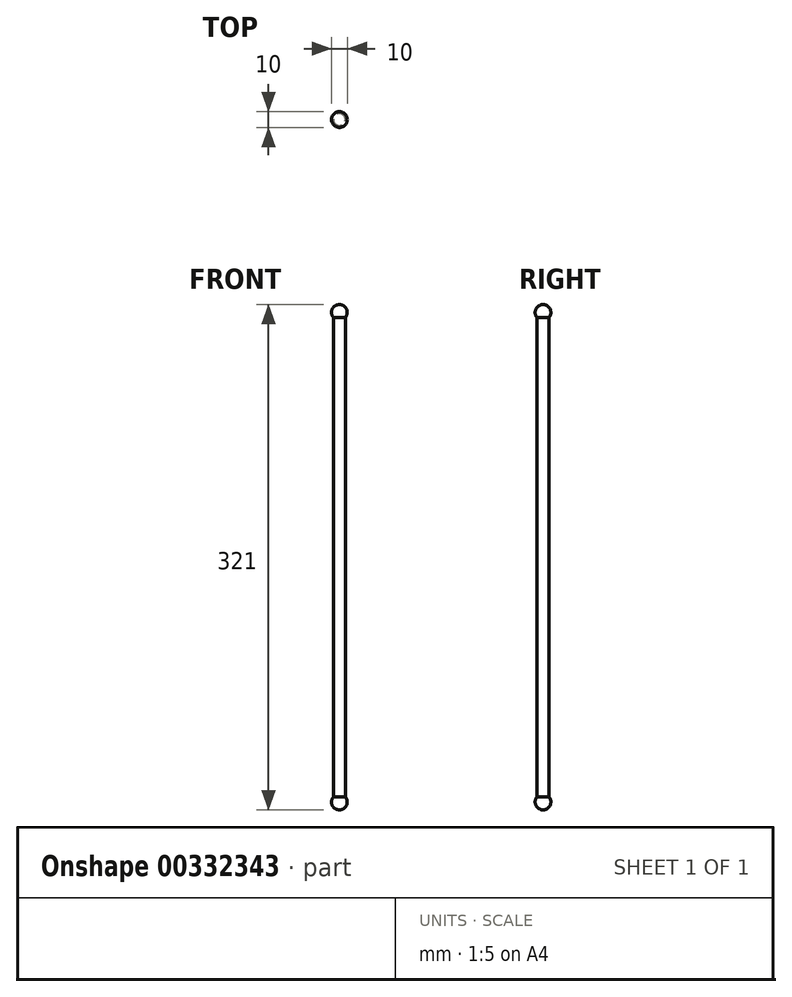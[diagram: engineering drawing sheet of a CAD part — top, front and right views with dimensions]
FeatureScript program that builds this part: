
annotation { "Feature Type Name" : "Feature", "Feature Type Description" : "" }
export const myFeature = defineFeature(function(context is Context, id is Id, definition is map)
    precondition{}
    {
        {
            var Q0;
            Q0=qCreatedBy(makeId("Top.planeOp"),FACE);
            var sketch = newSketch(context, id + "F0", { "sketchPlane" : qUnion([Q0])});
            skCircle(sketch, "E0", {"center": v(0, 0) * mm, "radius": 3.8 * mm});
            skSolve(sketch);
        }
        {
            var Q0;
            Q0=makeQuery(id+"F0.imprint","IMPRINT",FACE,{"disambiguationData":[TD([[makeQuery(id+"F0.imprint","IMPRINT",EDGE,{"derivedFrom":sQuery(id+"F0.wireOp",EDGE,"E0")}),1.0]])]});
            extrude(context, id + "F1", {"entities" : qUnion([Q0]), "depth" : 305 * mm});
        }
        {
            var Q0;
            Q0=makeQuery(id+"F1.opExtrude","CAP_FACE",FACE,{"disambiguationData":[OSD([sQuery(id+"F0.wireOp",EDGE,"E0")])],"isStart":false});
            cPlane(context, id + "F2", {"entities" : qUnion([Q0]), "cplaneType" : CPlaneType.OFFSET, "offset" : 3 * mm, "width" : 150 * mm, "height" : 150 * mm});
        }
        {
            var Q0;
            Q0=qCreatedBy(id+"F2.planeOp",FACE);
            var sketch = newSketch(context, id + "F3", { "sketchPlane" : qUnion([Q0])});
            skCircle(sketch, "E1", {"center": v(0, 0) * mm, "radius": 5 * mm});
            skLineSegment(sketch, "E2", {"start": v(0, 5) * mm, "end": v(0, -5) * mm});
            skSolve(sketch);
        }
        {
            var Q0;
            {var subQ0=sQuery(id+"F3.wireOp",EDGE,"E2");Q0=makeQuery(id+"F3.imprint","IMPRINT",FACE,{"disambiguationData":[TD([[makeQuery(id+"F3.imprint","IMPRINT",EDGE,{"derivedFrom":subQ0}),-1.0]])]});}
            var Q1;
            Q1=sQuery(id+"F3.wireOp",EDGE,"E2");
            revolve(context, id + "F4", {"operationType" : NewBodyOperationType.ADD, "entities" : qUnion([Q0]), "axis" : qUnion([Q1]), "revolveType" : RevolveType.FULL});
        }
        {
            var Q0;
            Q0=makeQuery(id+"F1.opExtrude","CAP_FACE",FACE,{"disambiguationData":[OSD([sQuery(id+"F0.wireOp",EDGE,"E0")])],"isStart":true});
            cPlane(context, id + "F5", {"entities" : qUnion([Q0]), "cplaneType" : CPlaneType.OFFSET, "offset" : 3 * mm, "width" : 150 * mm, "height" : 150 * mm});
        }
        {
            var Q0;
            Q0=qCreatedBy(id+"F5.planeOp",FACE);
            var sketch = newSketch(context, id + "F6", { "sketchPlane" : qUnion([Q0])});
            skCircle(sketch, "E3", {"center": v(0, 0) * mm, "radius": 5 * mm});
            skLineSegment(sketch, "E4", {"start": v(0, 5) * mm, "end": v(0, -5) * mm});
            skSolve(sketch);
        }
        {
            var Q0;
            {var subQ0=sQuery(id+"F6.wireOp",EDGE,"E4");Q0=makeQuery(id+"F6.imprint","IMPRINT",FACE,{"disambiguationData":[TD([[makeQuery(id+"F6.imprint","IMPRINT",EDGE,{"derivedFrom":subQ0}),-1.0]])]});}
            var Q1;
            Q1=sQuery(id+"F6.wireOp",EDGE,"E4");
            revolve(context, id + "F7", {"operationType" : NewBodyOperationType.ADD, "entities" : qUnion([Q0]), "axis" : qUnion([Q1]), "revolveType" : RevolveType.FULL});
        }
    });
